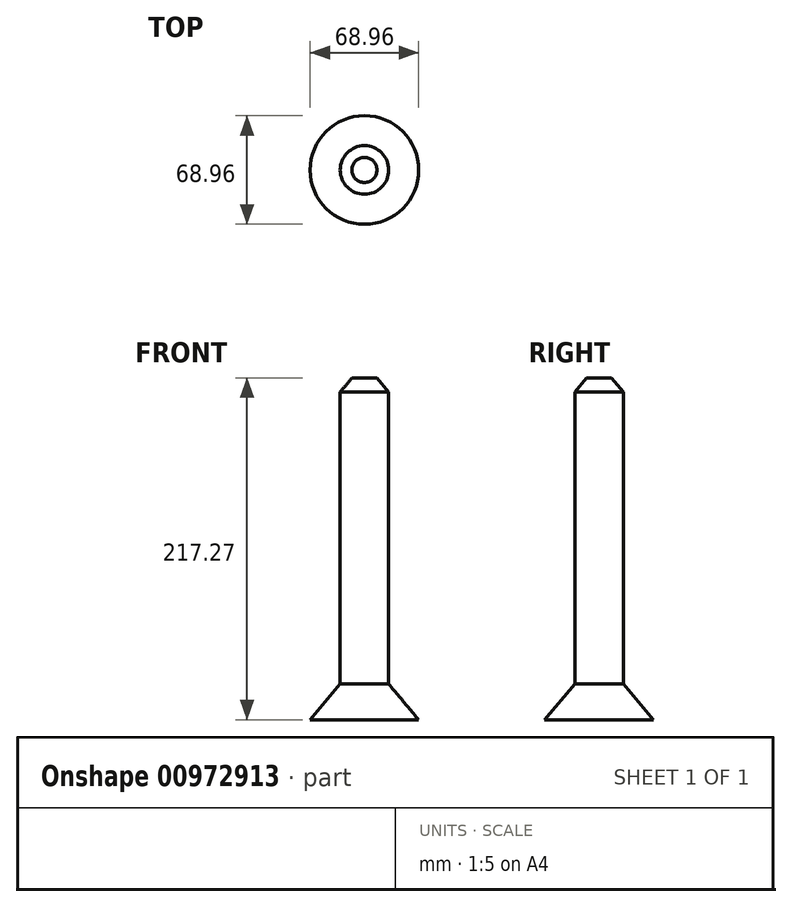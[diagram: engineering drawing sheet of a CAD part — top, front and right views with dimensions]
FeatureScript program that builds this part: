
annotation { "Feature Type Name" : "Feature", "Feature Type Description" : "" }
export const myFeature = defineFeature(function(context is Context, id is Id, definition is map)
    precondition{}
    {
        {
            var Q0;
            Q0=qCreatedBy(makeId("Top.planeOp"),FACE);
            var sketch = newSketch(context, id + "F0", { "sketchPlane" : qUnion([Q0])});
            skCircle(sketch, "E0", {"center": v(0, 0) * mm, "radius": 34.48 * mm});
            skSolve(sketch);
        }
        {
            var Q0;
            Q0=makeQuery(id+"F0.imprint","IMPRINT",FACE,{"disambiguationData":[TD([[makeQuery(id+"F0.imprint","IMPRINT",EDGE,{"derivedFrom":sQuery(id+"F0.wireOp",EDGE,"E0")}),1.0]])]});
            var Q1;
            Q1=sQuery(id+"F0.wireOp",EDGE,"E0");
            extrude(context, id + "F1", {"entities" : qUnion([Q0]), "surfaceEntities" : qUnion([Q1]), "depth" : 25.4 * mm, "offsetDistance" : 25.4 * mm, "hasDraft" : true, "draftAngle" : 40 * degree, "draftPullDirection" : true});
        }
        {
            var Q0;
            Q0=qCreatedBy(makeId("Top.planeOp"),FACE);
            var sketch = newSketch(context, id + "F2", { "sketchPlane" : qUnion([Q0])});
            skCircle(sketch, "E1", {"center": v(0, 0) * mm, "radius": 15.42 * mm});
            skSolve(sketch);
        }
        {
            var Q0;
            Q0 = qSketchRegion(id + "F2", true);
            extrude(context, id + "F3", {"entities" : qUnion([Q0]), "operationType" : NewBodyOperationType.ADD, "depth" : 217.27 * mm, "offsetDistance" : 25.4 * mm});
        }
        {
            var Q0;
            Q0=qCreatedBy(makeId("Right.planeOp"),FACE);
            var sketch = newSketch(context, id + "F4", { "sketchPlane" : qUnion([Q0])});
            skLineSegment(sketch, "E2", {"start": v(7.98, 217.23) * mm, "end": v(15.57, 207.91) * mm});
            skLineSegment(sketch, "E3", {"start": v(15.57, 207.91) * mm, "end": v(24.68, 207.91) * mm});
            skLineSegment(sketch, "E4", {"start": v(24.68, 207.91) * mm, "end": v(24.68, 224.61) * mm});
            skLineSegment(sketch, "E5", {"start": v(24.68, 224.61) * mm, "end": v(9.26, 224.61) * mm});
            skLineSegment(sketch, "E6", {"start": v(9.26, 224.61) * mm, "end": v(7.98, 217.23) * mm});
            skPoint(sketch, "E7.start.orphan", {"position": v(0, 217.23) * mm});
            skLineSegment(sketch, "E8", {"start": v(0, 217.23) * mm, "end": v(0, 238.22) * mm});
            skSolve(sketch);
        }
        {
            var Q0;
            Q0=makeQuery(id+"F4.imprint","IMPRINT",FACE,{"disambiguationData":[TD([[makeQuery(id+"F4.imprint","IMPRINT",EDGE,{"derivedFrom":sQuery(id+"F4.wireOp",EDGE,"E2")}),1.0]])]});
            var Q1;
            Q1=sQuery(id+"F4.wireOp",EDGE,"E8");
            revolve(context, id + "F5", {"operationType" : NewBodyOperationType.REMOVE, "surfaceOperationType" : NewSurfaceOperationType.NEW, "entities" : qUnion([Q0]), "axis" : qUnion([Q1]), "revolveType" : RevolveType.FULL, "oppositeDirection" : true});
        }
    });
